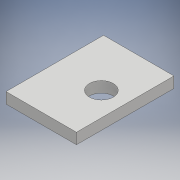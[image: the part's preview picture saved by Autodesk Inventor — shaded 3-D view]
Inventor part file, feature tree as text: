
AUTODESK INVENTOR PART (.ipt)
format: ipt  version: 2017 SP1 (Build 210196100, 196)  size: 98,816 bytes
history: native  units: mm
features: extrude x2, sketch x2
ambient origin geometry x8: Origin, YZ Plane, XZ Plane, XY Plane, X Axis, Y Axis, Z Axis, Center Point
bodies: Solide1 (feature_tree)
feature tree (4):
  extrude  "Extrusion1"  Depth=90.0mm
  extrude  "Extrusion2"  Depth=65.0mm
  sketch  "Esquisse1"
  sketch  "Esquisse2"
